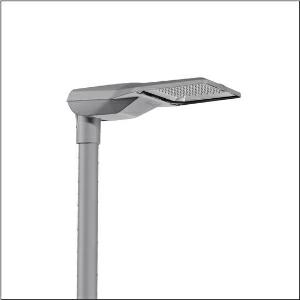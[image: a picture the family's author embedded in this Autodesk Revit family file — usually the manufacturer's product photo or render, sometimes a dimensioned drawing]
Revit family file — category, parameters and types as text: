
# Revit family: streetlight_sl_21_iq_midi___st0_5a_5xe3b31g08mb_2812
name_source: partatom
category: Lighting Fixtures
units: mm (PartAtom-declared; Revit-internal decimal feet)

## family parameters
Cut with Voids When Loaded = No
Host = Face
Light Source = No
Part Type = Normal
Room Calculation Point = No
Round Connector Dimension = Use Diameter
Shared = No

## types (1)
- --- (1 x LED, 19500 lm, 146.7 W, 3000K)
    Apparent Load = 147 VA
    CIE Flux Codes = 41 75 97 100 100
    Color Rendering = 70
    Color Temperature = 3000K
    Default Elevation = 1800 mm
    Description = Streetlight SL 21 iQ midi, mast luminaire, primary light control with lens, of PMMA, primary optical cover: cover, of toughened safety glass, transparent, light distribution: ST0.5a, light emission: direct distribution, primary light characteristic: asymmetric, installation type: post-top, side-entry, LED, High Power LED, rated luminous flux: 19.500lm, luminous efficacy: 133lm/W, light colour: 730, colour temperature: 3000K, control: Street-Remote, Auto-Match, Temp-Guard, Lumen-Switch, Night-Set, Smart-Wire, Light-Fading, Desk-Remote (wireless, voltage-free reading and setting of iQ features in the workshop via application-optimized NFC function/RFID function), optimised constant luminous flux control (CLO 2.0), pre-setting: linear dimming characteristic, mains connection: 230..240V, AC, 50/60Hz, start of lifetime: 147W, end of service life: 161W, reduction: 62W, luminaire housing, of diecast aluminium, powder-coated, Siteco® metallic grey (DB 702S), corrosivity category C5 mid according to DIN EN ISO 12944, please order mast flange separately, inclination adjustable: 0°, 5°, 10°, 15°, sealing non-destructively replaceable, multi-level sealing system, length: 644mm, width: 335mm, height: 110mm, mast flange for spigot size: 42mm (side-entry): 5XC10008XM4, 60/48mm (side-entry/post-top): 5XC10108XM2, 76/60mm (side-entry/post-top): 5XC10108XM1, protection rating (complete): IP66, insulation class (complete): insulation class II (safety insulation), certification: CE, ENEC, ENEC+, VDE, impact resistance: IK09, permissible operating ambient temperature for outdoor applications: -40..+50°C, standard-compliant lighting for roads and squares, packaging unit: 1 piece

Light Distribution: ST0.5a
    Height = 111 mm
    Lamp = 1 x LED
    Lamp Light Flux = 19500 lm
    Lamp Power = 146.7 W
    Lamp count = 1
    Length = 644 mm
    Luminous efficacy = 133 lm/W
    Manufacturer = Siteco
    ModVariant = No
    Model = 5XE3B31G08MB
    Number of Poles = 1
    OnlyDefault = Yes
    Power Factor = 1
    Product Name = Streetlight SL 21 iQ midi | ST0.5a
    Product group = mast luminaire | pylon top
    ProductGroupID = 6100
    Protection Class = Protection class II
    Protection Degree = IP 66
    RLX_Detail_Level = 1
    RLX_Emergency_Light_Flux = 0 lm
    RLX_Emergency_Type = 0
    RLX_Emergency_Type_DB = No
    RlxData = <blob elided: 102141 chars, md5=49e3fed6>
    Socket = socket
    Standby Power = 0 W
    System Light Flux = 19499 lm
    System Power = 147 W
    Type Comments = factory setting: luminous flux: 100 % | dim-lin: 254 | 753 mA
    Type Image = l_1004298.jpg
    URL = http://relux.com
    VarID = @adj_164519
    Voltage = 0 V
    Weight = 0.00 kg
    Width = 336 mm

## geometry (parser evidence)
native form markers: Blend x4, Sweep x10
no freeform markers — native parametric forms only
